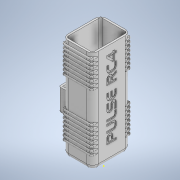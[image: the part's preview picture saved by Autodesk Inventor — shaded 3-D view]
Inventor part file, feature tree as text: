
AUTODESK INVENTOR PART (.ipt)
format: ipt  version: 2021 (Build 250183000, 183)  size: 1,127,424 bytes
history: native  units: mm
features: extrude x14, sketch x13, plane x7, mirror x6, fillet x6, projected_geometry x2, other x1
ambient origin geometry x8: Origin, YZ Plane, XZ Plane, XY Plane, X Axis, Y Axis, Z Axis, Center Point
bodies: Body1 (feature_tree)
feature tree (49):
  other  "Sólido1"
  extrude  "Extrusión1"  Depth=36.5mm
  extrude  "Extrusión2"  Depth=6.0mm
  extrude  "Extrusión3"  Depth=2.0mm
  plane  "Plano de trabajo1"
  mirror  "Simetría1"
  fillet  "Empalme1"  Radius=108.0mm
  plane  "Plano de trabajo2"
  extrude  "Extrusión4"  Depth=8.0mm
  plane  "Plano de trabajo3"
  mirror  "Simetría2"
  plane  "Plano de trabajo4"
  mirror  "Simetría3"
  plane  "Plano de trabajo5"
  mirror  "Simetría4"
  plane  "Plano de trabajo6"
  mirror  "Simetría5"
  plane  "Plano de trabajo8"
  mirror  "Simetría6"
  fillet  "Empalme2"  Radius=2.0mm
  fillet  "Empalme3"  Radius=2.0mm
  sketch  "Boceto4"  dims[d4=2.0mm d5=2.0mm d6=108.0mm d7=0.0mm]
  extrude  "Extrusión5"  Depth=2.0mm TaperAngle=0.0deg
  extrude  "Extrusión6"  Depth=6.0mm
  extrude  "Extrusión7"  Depth=11.0mm
  extrude  "Extrusión8"  [1 undecoded]
  extrude  "Extrusión9"  Depth=2.0mm
  fillet  "Empalme4"  Radius=2.0mm
  extrude  "Extrusión10"  [1 undecoded]
  extrude  "Extrusión11"  [1 undecoded]
  extrude  "Extrusión12"  Depth=1.0mm
  extrude  "Extrusión13"  Depth=9.0mm
  fillet  "Empalme6"  Radius=4.15mm
  extrude  "Extrusión14"  Depth=9.0mm
  fillet  "Empalme7"  Radius=24.0mm
  sketch  "Boceto2"  dims[d0=27.85mm d1=36.5mm]
  sketch  "Boceto3"  dims[d2=2.0mm d3=6.0mm]
  sketch  "Boceto5"  dims[d8=2.0mm d9=0.0mm d10=8.0mm d11=2.0mm d12=2.0mm]
  sketch  "Boceto6"  dims[d13=2.0mm d14=2.0mm d15=0.0mm]
  sketch  "Boceto7"  dims[d16=20.0mm d17=6.0mm]
  sketch  "Boceto8"  dims[d18=3.2mm d19=11.0mm]
  projected_geometry  "Contorno proyectado1"
  sketch  "Boceto9"  dims[d20=5.0mm d21=-4.0mm]
  sketch  "Boceto10"  dims[d22=1.0mm d23=2.0mm d24=2.0mm d25=0.0mm]
  sketch  "Boceto11"  dims[d26=-3.0mm d27=-4.0mm]
  sketch  "Boceto12"  dims[d28=-8.0mm d29=-30.0mm]
  sketch  "Boceto13"  dims[d30=1.0mm d31=1.0mm]
  projected_geometry  "Contorno proyectado2"
  sketch  "Boceto14"  dims[d32=1.0mm d33=0.0mm d37=20.0mm d38=4.15mm d39=4.35mm d40=24.0mm d41=14.0mm d42=0.0mm d43=8.0mm d44=0.0mm d45=7.0mm d46=2.0mm d47=15.0mm d48=0.0mm d49=2.0mm d50=7.0mm d51=0.0mm d52=2.0mm d53=6.0mm d54=0.0mm d56=14.0mm d57=0.0mm d58=8.0mm d59=0.0mm d60=8.0mm d61=0.0mm d62=2.0mm d63=8.0mm d64=0.0mm d65=75.0mm d66=75.0mm d67=16.5mm d68=11.273282mm d70=8.0mm d71=2.0mm d72=9.0mm d73=9.0mm]
note: 3 required parameter values undecoded (feature->parameter linkage not recoverable at this tier; creation-order binding heuristic only, values carry confidence <= 0.55)
